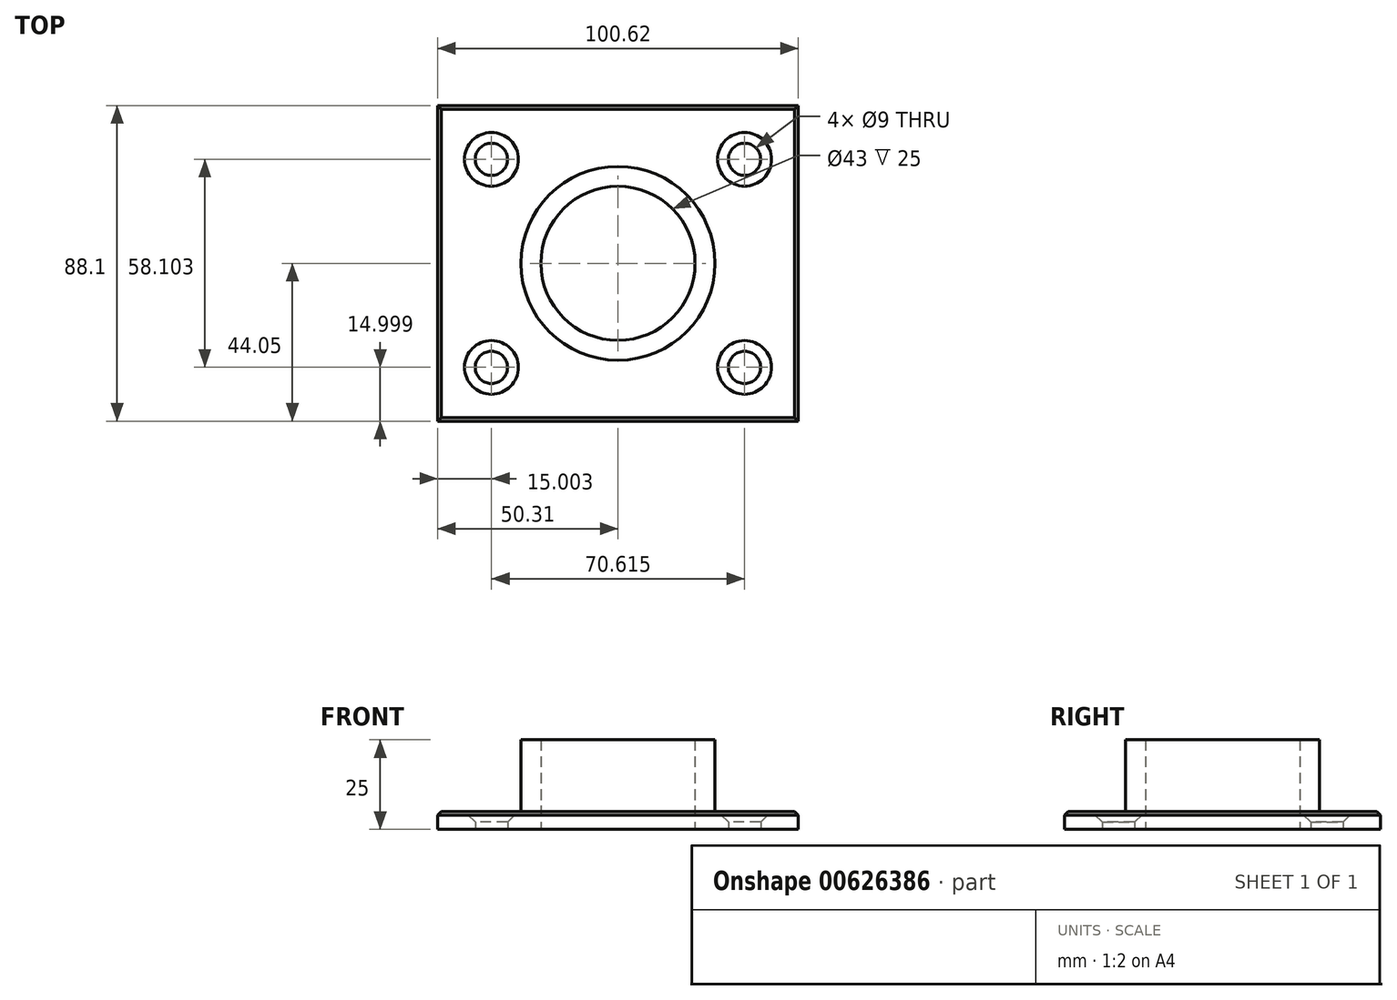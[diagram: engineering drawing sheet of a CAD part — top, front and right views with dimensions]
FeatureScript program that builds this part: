
annotation { "Feature Type Name" : "Feature", "Feature Type Description" : "" }
export const myFeature = defineFeature(function(context is Context, id is Id, definition is map)
    precondition{}
    {
        {
            var Q0;
            Q0=qCreatedBy(makeId("Top.planeOp"),FACE);
            var sketch = newSketch(context, id + "F0", { "sketchPlane" : qUnion([Q0])});
            skCircle(sketch, "E0", {"center": v(0, 0) * mm, "radius": 27.06 * mm});
            skLineSegment(sketch, "E1.bottom", {"start": v(50.3, 44.05) * mm, "end": v(-50.3, 44.05) * mm});
            skLineSegment(sketch, "E1.top", {"start": v(50.3, -44.05) * mm, "end": v(-50.3, -44.05) * mm});
            skLineSegment(sketch, "E1.left", {"start": v(50.3, 44.05) * mm, "end": v(50.3, -44.05) * mm});
            skLineSegment(sketch, "E1.right", {"start": v(-50.3, 44.05) * mm, "end": v(-50.3, -44.05) * mm});
            skSolve(sketch);
        }
        {
            var Q0;
            Q0=makeQuery(id+"F0.imprint","IMPRINT",FACE,{"disambiguationData":[TD([[makeQuery(id+"F0.imprint","IMPRINT",EDGE,{"derivedFrom":sQuery(id+"F0.wireOp",EDGE,"E0")}),1.0]])]});
            extrude(context, id + "F1", {"entities" : qUnion([Q0]), "depth" : 25 * mm, "offsetDistance" : 25 * mm});
        }
        {
            var Q0;
            Q0=makeQuery(id+"F0.imprint","IMPRINT",FACE,{"disambiguationData":[TD([[makeQuery(id+"F0.imprint","IMPRINT",EDGE,{"derivedFrom":sQuery(id+"F0.wireOp",EDGE,"E0")}),-1.0]])]});
            extrude(context, id + "F2", {"entities" : qUnion([Q0]), "operationType" : NewBodyOperationType.ADD, "depth" : 5 * mm, "offsetDistance" : 25 * mm});
        }
        {
            var Q0;
            Q0=makeQuery(id+"F2.opExtrude","CAP_EDGE",EDGE,{"disambiguationData":[OSD([sQuery(id+"F0.wireOp",EDGE,"E1.right")])],"isStart":false});
            var Q1;
            Q1=makeQuery(id+"F2.opExtrude","CAP_EDGE",EDGE,{"disambiguationData":[OSD([sQuery(id+"F0.wireOp",EDGE,"E1.top")])],"isStart":false});
            var Q2;
            Q2=makeQuery(id+"F2.opExtrude","CAP_EDGE",EDGE,{"disambiguationData":[OSD([sQuery(id+"F0.wireOp",EDGE,"E1.left")])],"isStart":false});
            var Q3;
            Q3=makeQuery(id+"F2.opExtrude","CAP_EDGE",EDGE,{"disambiguationData":[OSD([sQuery(id+"F0.wireOp",EDGE,"E1.bottom")])],"isStart":false});
            chamfer(context, id + "F3", {"entities" : qUnion([Q0, Q1, Q2, Q3]), "width" : 1 * mm, "tangentPropagation" : true});
        }
        {
            var Q0;
            Q0=qCreatedBy(makeId("Top.planeOp"),FACE);
            var sketch = newSketch(context, id + "F4", { "sketchPlane" : qUnion([Q0])});
            skCircle(sketch, "E2", {"center": v(0, 0) * mm, "radius": 21.5 * mm});
            skSolve(sketch);
        }
        {
            var Q0;
            Q0 = qSketchRegion(id + "F4", true);
            extrude(context, id + "F5", {"entities" : qUnion([Q0]), "operationType" : NewBodyOperationType.REMOVE, "depth" : 30 * mm, "offsetDistance" : 25 * mm});
        }
        {
            var Q0;
            Q0=qCreatedBy(makeId("Top.planeOp"),FACE);
            var sketch = newSketch(context, id + "F6", { "sketchPlane" : qUnion([Q0])});
            skCircle(sketch, "E3", {"center": v(35.3, -29.05) * mm, "radius": 4.5 * mm});
            skCircle(sketch, "E4", {"center": v(35.3, 29.05) * mm, "radius": 4.5 * mm});
            skCircle(sketch, "E5", {"center": v(-35.3, 29.05) * mm, "radius": 4.5 * mm});
            skCircle(sketch, "E6", {"center": v(-35.3, -29.05) * mm, "radius": 4.5 * mm});
            skSolve(sketch);
        }
        {
            var Q0;
            Q0 = qSketchRegion(id + "F6", true);
            extrude(context, id + "F7", {"entities" : qUnion([Q0]), "operationType" : NewBodyOperationType.REMOVE, "endBound" : BoundingType.SYMMETRIC, "depth" : 25 * mm, "offsetDistance" : 25 * mm});
        }
        {
            var Q0;
            Q0=makeQuery(id+"F7.boolean.opBoolean","INTERSECT",EDGE,{"derivedFrom":[makeQuery(id+"F2.opExtrude","CAP_FACE",FACE,{"disambiguationData":[OSD([sQuery(id+"F0.wireOp",EDGE,"E0"),sQuery(id+"F0.wireOp",EDGE,"E1.bottom"),sQuery(id+"F0.wireOp",EDGE,"E1.top"),sQuery(id+"F0.wireOp",EDGE,"E1.left"),sQuery(id+"F0.wireOp",EDGE,"E1.right")])],"isStart":false}),makeQuery(id+"F7.opExtrude","SWEPT_FACE",FACE,{"disambiguationData":[OSD([sQuery(id+"F6.wireOp",EDGE,"E6")])]})]});
            var Q1;
            Q1=makeQuery(id+"F7.boolean.opBoolean","INTERSECT",EDGE,{"derivedFrom":[makeQuery(id+"F2.opExtrude","CAP_FACE",FACE,{"disambiguationData":[OSD([sQuery(id+"F0.wireOp",EDGE,"E0"),sQuery(id+"F0.wireOp",EDGE,"E1.bottom"),sQuery(id+"F0.wireOp",EDGE,"E1.top"),sQuery(id+"F0.wireOp",EDGE,"E1.left"),sQuery(id+"F0.wireOp",EDGE,"E1.right")])],"isStart":false}),makeQuery(id+"F7.opExtrude","SWEPT_FACE",FACE,{"disambiguationData":[OSD([sQuery(id+"F6.wireOp",EDGE,"E5")])]})]});
            var Q2;
            Q2=makeQuery(id+"F7.boolean.opBoolean","INTERSECT",EDGE,{"derivedFrom":[makeQuery(id+"F2.opExtrude","CAP_FACE",FACE,{"disambiguationData":[OSD([sQuery(id+"F0.wireOp",EDGE,"E0"),sQuery(id+"F0.wireOp",EDGE,"E1.bottom"),sQuery(id+"F0.wireOp",EDGE,"E1.top"),sQuery(id+"F0.wireOp",EDGE,"E1.left"),sQuery(id+"F0.wireOp",EDGE,"E1.right")])],"isStart":false}),makeQuery(id+"F7.opExtrude","SWEPT_FACE",FACE,{"disambiguationData":[OSD([sQuery(id+"F6.wireOp",EDGE,"E4")])]})]});
            var Q3;
            Q3=makeQuery(id+"F7.boolean.opBoolean","INTERSECT",EDGE,{"derivedFrom":[makeQuery(id+"F2.opExtrude","CAP_FACE",FACE,{"disambiguationData":[OSD([sQuery(id+"F0.wireOp",EDGE,"E0"),sQuery(id+"F0.wireOp",EDGE,"E1.bottom"),sQuery(id+"F0.wireOp",EDGE,"E1.top"),sQuery(id+"F0.wireOp",EDGE,"E1.left"),sQuery(id+"F0.wireOp",EDGE,"E1.right")])],"isStart":false}),makeQuery(id+"F7.opExtrude","SWEPT_FACE",FACE,{"disambiguationData":[OSD([sQuery(id+"F6.wireOp",EDGE,"E3")])]})]});
            chamfer(context, id + "F8", {"entities" : qUnion([Q0, Q1, Q2, Q3]), "width" : 3 * mm, "tangentPropagation" : true});
        }
    });
